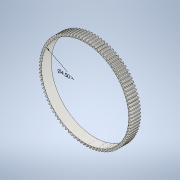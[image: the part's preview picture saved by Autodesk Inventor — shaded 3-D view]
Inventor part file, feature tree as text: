
AUTODESK INVENTOR PART (.ipt)
format: ipt  version: 2022.1 (Build 261234020, 234B)  size: 544,768 bytes
history: native  units: mm (DEFAULTED — no unit token found)
features: other x5, plane x3, sketch x3, extrude x2
ambient origin geometry x8: Origin, YZ Plane, XZ Plane, XY Plane, X Axis, Y Axis, Z Axis, Center Point
bodies: Solid1 (feature_tree)
feature tree (13):
  other  "Annotations"
  extrude  "Extrusion1"  Depth=12.7mm TaperAngle=0.0deg
  plane  "Work Plane1"
  plane  "Work Plane2"
  plane  "Work Plane3"
  other  "Spur Gear"
  extrude  "Extrusion2"  Depth=76.2mm TaperAngle=0.0deg
  sketch  "Sketch1"  dims[d0=120.65mm d1=12.7mm d2=0.0mm]
  sketch  "Sketch2"  dims[d3=118.11mm d4=76.2mm d5=0.0mm]
  other  "Srf1"
  sketch  "Sketch4"  dims[d6=0.0mm d7=0.337806mm d9=0.0mm d14=0.0mm d15=71.755mm d16=0.0mm d17=0.0mm d18=0.0mm d19=71.755mm d21=114.3mm d22=0.0mm d23=0.0mm d27=26.66135mm d28=114.3mm]
  other  "Pitch Diameter"
  other  "Diameter Dimension 1"
